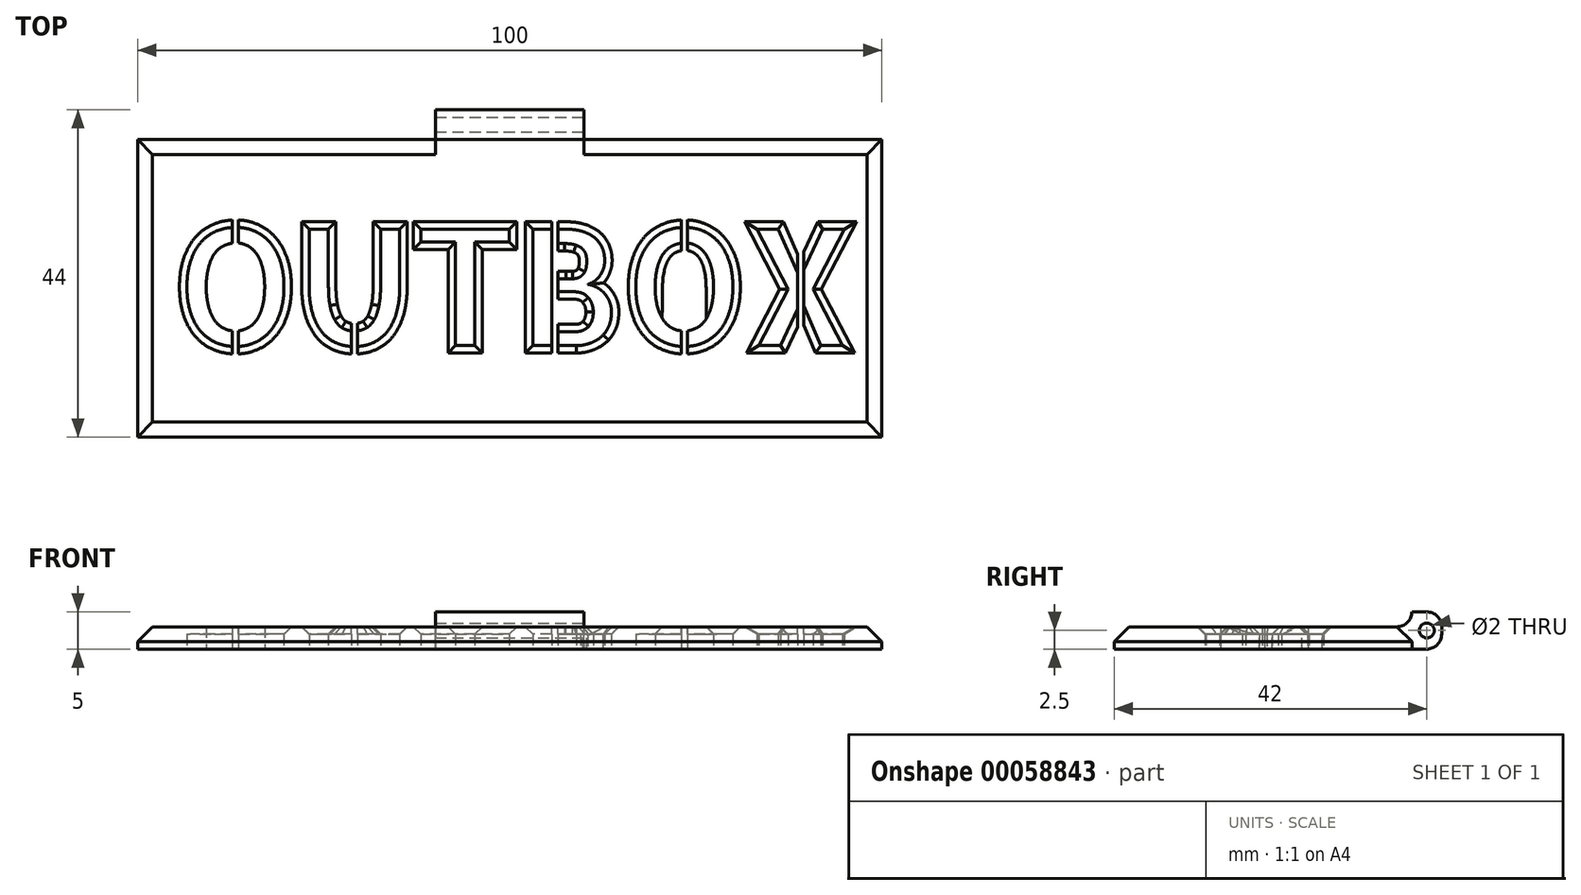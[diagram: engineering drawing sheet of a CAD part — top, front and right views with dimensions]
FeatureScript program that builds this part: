
annotation { "Feature Type Name" : "Feature", "Feature Type Description" : "" }
export const myFeature = defineFeature(function(context is Context, id is Id, definition is map)
    precondition{}
    {
        {
            var Q0;
            Q0=qCreatedBy(makeId("Top.planeOp"),FACE);
            var sketch = newSketch(context, id + "F0", { "sketchPlane" : qUnion([Q0])});
            skLineSegment(sketch, "E0.rect.bottom", {"start": v(-50, 20) * mm, "end": v(-10, 20) * mm});
            skLineSegment(sketch, "E0.rect.top", {"start": v(-50, -20) * mm, "end": v(50, -20) * mm});
            skLineSegment(sketch, "E0.rect.left", {"start": v(-50, 20) * mm, "end": v(-50, -20) * mm});
            skLineSegment(sketch, "E0.rect.right", {"start": v(50, 20) * mm, "end": v(50, -20) * mm});
            skPoint(sketch, "E0.rect.middle", {"position": v(0, 0) * mm});
            skText(sketch, "E1", { "text": "OUTBOX", "fontName": "AllertaStencil-Regular.ttf"});
            skLineSegment(sketch, "E2.rect.bottom", {"start": v(-10, 24) * mm, "end": v(10, 24) * mm});
            skLineSegment(sketch, "E2.rect.left", {"start": v(-10, 24) * mm, "end": v(-10, 20) * mm});
            skLineSegment(sketch, "E2.rect.right", {"start": v(10, 24) * mm, "end": v(10, 20) * mm});
            skPoint(sketch, "E2.rect.middle", {"position": v(0, 20) * mm});
            skPoint(sketch, "E2.rect.top.start.orphan", {"position": v(-10, 16) * mm});
            skPoint(sketch, "E3.orphan", {"position": v(10, 16) * mm});
            skLineSegment(sketch, "E4.trimOffspring", {"start": v(10, 20) * mm, "end": v(50, 20) * mm});
            skLineSegment(sketch, "E5", {"start": v(10, 20) * mm, "end": v(-10, 20) * mm});
            const initialGuessF0  = {"E1": [-0.045, -0.00771, 1, 0, 0.01566]};
            skSetInitialGuess(sketch, initialGuessF0);
            skSolve(sketch);
        }
        {
            var Q0;
            Q0 = qSketchRegion(id + "F0", true);
            extrude(context, id + "F1", {"entities" : qUnion([Q0]), "depth" : 3 * mm});
        }
        {
            var Q0;
            Q0=makeQuery(id+"F0.imprint","IMPRINT",FACE,{"disambiguationData":[TD([[makeQuery(id+"F0.imprint","IMPRINT",EDGE,{"derivedFrom":sQuery(id+"F0.wireOp",EDGE,"E2.rect.bottom")}),-1.0]])]});
            extrude(context, id + "F2", {"entities" : qUnion([Q0]), "operationType" : NewBodyOperationType.ADD, "depth" : 5 * mm});
        }
        {
            var Q0;
            Q0=makeQuery(id+"F2.boolean.opBoolean","INTERSECT",EDGE,{"derivedFrom":[makeQuery(id+"F1.opExtrude","CAP_FACE",FACE,{"disambiguationData":[OSD([sQuery(id+"F0.wireOp",EDGE,"E0.rect.bottom"),sQuery(id+"F0.wireOp",EDGE,"E0.rect.top"),sQuery(id+"F0.wireOp",EDGE,"E0.rect.left"),sQuery(id+"F0.wireOp",EDGE,"E0.rect.right"),sQuery(id+"F0.wireOp",EDGE,"E1.sketch_text.stroke-0"),sQuery(id+"F0.wireOp",EDGE,"E1.sketch_text.stroke-1"),sQuery(id+"F0.wireOp",EDGE,"E1.sketch_text.stroke-2"),sQuery(id+"F0.wireOp",EDGE,"E1.sketch_text.stroke-3"),sQuery(id+"F0.wireOp",EDGE,"E1.sketch_text.stroke-4"),sQuery(id+"F0.wireOp",EDGE,"E1.sketch_text.stroke-5"),sQuery(id+"F0.wireOp",EDGE,"E1.sketch_text.stroke-6"),sQuery(id+"F0.wireOp",EDGE,"E1.sketch_text.stroke-7"),sQuery(id+"F0.wireOp",EDGE,"E1.sketch_text.stroke-8"),sQuery(id+"F0.wireOp",EDGE,"E1.sketch_text.stroke-9"),sQuery(id+"F0.wireOp",EDGE,"E1.sketch_text.stroke-10"),sQuery(id+"F0.wireOp",EDGE,"E1.sketch_text.stroke-11"),sQuery(id+"F0.wireOp",EDGE,"E1.sketch_text.stroke-12"),sQuery(id+"F0.wireOp",EDGE,"E1.sketch_text.stroke-13"),sQuery(id+"F0.wireOp",EDGE,"E1.sketch_text.stroke-14"),sQuery(id+"F0.wireOp",EDGE,"E1.sketch_text.stroke-15"),sQuery(id+"F0.wireOp",EDGE,"E1.sketch_text.stroke-16"),sQuery(id+"F0.wireOp",EDGE,"E1.sketch_text.stroke-17"),sQuery(id+"F0.wireOp",EDGE,"E1.sketch_text.stroke-18"),sQuery(id+"F0.wireOp",EDGE,"E1.sketch_text.stroke-19"),sQuery(id+"F0.wireOp",EDGE,"E1.sketch_text.stroke-20"),sQuery(id+"F0.wireOp",EDGE,"E1.sketch_text.stroke-21"),sQuery(id+"F0.wireOp",EDGE,"E1.sketch_text.stroke-22"),sQuery(id+"F0.wireOp",EDGE,"E1.sketch_text.stroke-23"),sQuery(id+"F0.wireOp",EDGE,"E1.sketch_text.stroke-24"),sQuery(id+"F0.wireOp",EDGE,"E1.sketch_text.stroke-25"),sQuery(id+"F0.wireOp",EDGE,"E1.sketch_text.stroke-26"),sQuery(id+"F0.wireOp",EDGE,"E1.sketch_text.stroke-27"),sQuery(id+"F0.wireOp",EDGE,"E1.sketch_text.stroke-28"),sQuery(id+"F0.wireOp",EDGE,"E1.sketch_text.stroke-29"),sQuery(id+"F0.wireOp",EDGE,"E1.sketch_text.stroke-30"),sQuery(id+"F0.wireOp",EDGE,"E1.sketch_text.stroke-31"),sQuery(id+"F0.wireOp",EDGE,"E1.sketch_text.stroke-32"),sQuery(id+"F0.wireOp",EDGE,"E1.sketch_text.stroke-33"),sQuery(id+"F0.wireOp",EDGE,"E1.sketch_text.stroke-34"),sQuery(id+"F0.wireOp",EDGE,"E1.sketch_text.stroke-35"),sQuery(id+"F0.wireOp",EDGE,"E1.sketch_text.stroke-36"),sQuery(id+"F0.wireOp",EDGE,"E1.sketch_text.stroke-37"),sQuery(id+"F0.wireOp",EDGE,"E1.sketch_text.stroke-38"),sQuery(id+"F0.wireOp",EDGE,"E1.sketch_text.stroke-39"),sQuery(id+"F0.wireOp",EDGE,"E1.sketch_text.stroke-40"),sQuery(id+"F0.wireOp",EDGE,"E1.sketch_text.stroke-41"),sQuery(id+"F0.wireOp",EDGE,"E1.sketch_text.stroke-42"),sQuery(id+"F0.wireOp",EDGE,"E1.sketch_text.stroke-43"),sQuery(id+"F0.wireOp",EDGE,"E1.sketch_text.stroke-44"),sQuery(id+"F0.wireOp",EDGE,"E1.sketch_text.stroke-45"),sQuery(id+"F0.wireOp",EDGE,"E1.sketch_text.stroke-46"),sQuery(id+"F0.wireOp",EDGE,"E1.sketch_text.stroke-47"),sQuery(id+"F0.wireOp",EDGE,"E1.sketch_text.stroke-48"),sQuery(id+"F0.wireOp",EDGE,"E1.sketch_text.stroke-49"),sQuery(id+"F0.wireOp",EDGE,"E1.sketch_text.stroke-50"),sQuery(id+"F0.wireOp",EDGE,"E1.sketch_text.stroke-51"),sQuery(id+"F0.wireOp",EDGE,"E1.sketch_text.stroke-52"),sQuery(id+"F0.wireOp",EDGE,"E1.sketch_text.stroke-53"),sQuery(id+"F0.wireOp",EDGE,"E1.sketch_text.stroke-54"),sQuery(id+"F0.wireOp",EDGE,"E1.sketch_text.stroke-55"),sQuery(id+"F0.wireOp",EDGE,"E1.sketch_text.stroke-56"),sQuery(id+"F0.wireOp",EDGE,"E1.sketch_text.stroke-57"),sQuery(id+"F0.wireOp",EDGE,"E1.sketch_text.stroke-58"),sQuery(id+"F0.wireOp",EDGE,"E1.sketch_text.stroke-59"),sQuery(id+"F0.wireOp",EDGE,"E1.sketch_text.stroke-60"),sQuery(id+"F0.wireOp",EDGE,"E1.sketch_text.stroke-61"),sQuery(id+"F0.wireOp",EDGE,"E1.sketch_text.stroke-62"),sQuery(id+"F0.wireOp",EDGE,"E1.sketch_text.stroke-63"),sQuery(id+"F0.wireOp",EDGE,"E1.sketch_text.stroke-64"),sQuery(id+"F0.wireOp",EDGE,"E1.sketch_text.stroke-65"),sQuery(id+"F0.wireOp",EDGE,"E1.sketch_text.stroke-66"),sQuery(id+"F0.wireOp",EDGE,"E1.sketch_text.stroke-67"),sQuery(id+"F0.wireOp",EDGE,"E1.sketch_text.stroke-68"),sQuery(id+"F0.wireOp",EDGE,"E1.sketch_text.stroke-69"),sQuery(id+"F0.wireOp",EDGE,"E1.sketch_text.stroke-70"),sQuery(id+"F0.wireOp",EDGE,"E1.sketch_text.stroke-71"),sQuery(id+"F0.wireOp",EDGE,"E1.sketch_text.stroke-72"),sQuery(id+"F0.wireOp",EDGE,"E1.sketch_text.stroke-73"),sQuery(id+"F0.wireOp",EDGE,"E1.sketch_text.stroke-74"),sQuery(id+"F0.wireOp",EDGE,"E1.sketch_text.stroke-75"),sQuery(id+"F0.wireOp",EDGE,"E1.sketch_text.stroke-76"),sQuery(id+"F0.wireOp",EDGE,"E1.sketch_text.stroke-77"),sQuery(id+"F0.wireOp",EDGE,"E1.sketch_text.stroke-78"),sQuery(id+"F0.wireOp",EDGE,"E1.sketch_text.stroke-79"),sQuery(id+"F0.wireOp",EDGE,"E1.sketch_text.stroke-80"),sQuery(id+"F0.wireOp",EDGE,"E1.sketch_text.stroke-81"),sQuery(id+"F0.wireOp",EDGE,"E1.sketch_text.stroke-82"),sQuery(id+"F0.wireOp",EDGE,"E1.sketch_text.stroke-83"),sQuery(id+"F0.wireOp",EDGE,"E1.sketch_text.stroke-84"),sQuery(id+"F0.wireOp",EDGE,"E1.sketch_text.stroke-85"),sQuery(id+"F0.wireOp",EDGE,"E1.sketch_text.stroke-86"),sQuery(id+"F0.wireOp",EDGE,"E1.sketch_text.stroke-87"),sQuery(id+"F0.wireOp",EDGE,"E1.sketch_text.stroke-88"),sQuery(id+"F0.wireOp",EDGE,"E1.sketch_text.stroke-89"),sQuery(id+"F0.wireOp",EDGE,"E1.sketch_text.stroke-90"),sQuery(id+"F0.wireOp",EDGE,"E1.sketch_text.stroke-91"),sQuery(id+"F0.wireOp",EDGE,"E1.sketch_text.stroke-92"),sQuery(id+"F0.wireOp",EDGE,"E1.sketch_text.stroke-93"),sQuery(id+"F0.wireOp",EDGE,"E1.sketch_text.stroke-94"),sQuery(id+"F0.wireOp",EDGE,"E1.sketch_text.stroke-95"),sQuery(id+"F0.wireOp",EDGE,"E1.sketch_text.stroke-96"),sQuery(id+"F0.wireOp",EDGE,"E1.sketch_text.stroke-97"),sQuery(id+"F0.wireOp",EDGE,"E1.sketch_text.stroke-98"),sQuery(id+"F0.wireOp",EDGE,"E1.sketch_text.stroke-99"),sQuery(id+"F0.wireOp",EDGE,"E1.sketch_text.stroke-100"),sQuery(id+"F0.wireOp",EDGE,"E1.sketch_text.stroke-101"),sQuery(id+"F0.wireOp",EDGE,"E1.sketch_text.stroke-102"),sQuery(id+"F0.wireOp",EDGE,"E1.sketch_text.stroke-103"),sQuery(id+"F0.wireOp",EDGE,"E1.sketch_text.stroke-104"),sQuery(id+"F0.wireOp",EDGE,"E1.sketch_text.stroke-105"),sQuery(id+"F0.wireOp",EDGE,"E1.sketch_text.stroke-106"),sQuery(id+"F0.wireOp",EDGE,"E1.sketch_text.stroke-107"),sQuery(id+"F0.wireOp",EDGE,"E1.sketch_text.stroke-108"),sQuery(id+"F0.wireOp",EDGE,"E1.sketch_text.stroke-109"),sQuery(id+"F0.wireOp",EDGE,"E1.sketch_text.stroke-110"),sQuery(id+"F0.wireOp",EDGE,"E1.sketch_text.stroke-111"),sQuery(id+"F0.wireOp",EDGE,"E1.sketch_text.stroke-112"),sQuery(id+"F0.wireOp",EDGE,"E1.sketch_text.stroke-113"),sQuery(id+"F0.wireOp",EDGE,"E1.sketch_text.stroke-114"),sQuery(id+"F0.wireOp",EDGE,"E1.sketch_text.stroke-115"),sQuery(id+"F0.wireOp",EDGE,"E1.sketch_text.stroke-116"),sQuery(id+"F0.wireOp",EDGE,"E1.sketch_text.stroke-117"),sQuery(id+"F0.wireOp",EDGE,"E1.sketch_text.stroke-118"),sQuery(id+"F0.wireOp",EDGE,"E1.sketch_text.stroke-119"),sQuery(id+"F0.wireOp",EDGE,"E1.sketch_text.stroke-120"),sQuery(id+"F0.wireOp",EDGE,"E1.sketch_text.stroke-121"),sQuery(id+"F0.wireOp",EDGE,"E1.sketch_text.stroke-122"),sQuery(id+"F0.wireOp",EDGE,"E1.sketch_text.stroke-123"),sQuery(id+"F0.wireOp",EDGE,"E1.sketch_text.stroke-124"),sQuery(id+"F0.wireOp",EDGE,"E1.sketch_text.stroke-125"),sQuery(id+"F0.wireOp",EDGE,"E1.sketch_text.stroke-126"),sQuery(id+"F0.wireOp",EDGE,"E1.sketch_text.stroke-127"),sQuery(id+"F0.wireOp",EDGE,"E1.sketch_text.stroke-128"),sQuery(id+"F0.wireOp",EDGE,"E1.sketch_text.stroke-129"),sQuery(id+"F0.wireOp",EDGE,"E1.sketch_text.stroke-130"),sQuery(id+"F0.wireOp",EDGE,"E1.sketch_text.stroke-131"),sQuery(id+"F0.wireOp",EDGE,"E1.sketch_text.stroke-132"),sQuery(id+"F0.wireOp",EDGE,"E1.sketch_text.stroke-133"),sQuery(id+"F0.wireOp",EDGE,"E1.sketch_text.stroke-134"),sQuery(id+"F0.wireOp",EDGE,"E1.sketch_text.stroke-135"),sQuery(id+"F0.wireOp",EDGE,"E1.sketch_text.stroke-136"),sQuery(id+"F0.wireOp",EDGE,"E1.sketch_text.stroke-137"),sQuery(id+"F0.wireOp",EDGE,"E1.sketch_text.stroke-138"),sQuery(id+"F0.wireOp",EDGE,"E1.sketch_text.stroke-139"),sQuery(id+"F0.wireOp",EDGE,"E1.sketch_text.stroke-140"),sQuery(id+"F0.wireOp",EDGE,"E1.sketch_text.stroke-141"),sQuery(id+"F0.wireOp",EDGE,"E1.sketch_text.stroke-142"),sQuery(id+"F0.wireOp",EDGE,"E1.sketch_text.stroke-143"),sQuery(id+"F0.wireOp",EDGE,"E1.sketch_text.stroke-144"),sQuery(id+"F0.wireOp",EDGE,"E1.sketch_text.stroke-145"),sQuery(id+"F0.wireOp",EDGE,"E1.sketch_text.stroke-146"),sQuery(id+"F0.wireOp",EDGE,"E1.sketch_text.stroke-147"),sQuery(id+"F0.wireOp",EDGE,"E1.sketch_text.stroke-148"),sQuery(id+"F0.wireOp",EDGE,"E1.sketch_text.stroke-149"),sQuery(id+"F0.wireOp",EDGE,"E1.sketch_text.stroke-150"),sQuery(id+"F0.wireOp",EDGE,"E1.sketch_text.stroke-151"),sQuery(id+"F0.wireOp",EDGE,"E1.sketch_text.stroke-152"),sQuery(id+"F0.wireOp",EDGE,"E1.sketch_text.stroke-153"),sQuery(id+"F0.wireOp",EDGE,"E1.sketch_text.stroke-154"),sQuery(id+"F0.wireOp",EDGE,"E1.sketch_text.stroke-155"),sQuery(id+"F0.wireOp",EDGE,"E1.sketch_text.stroke-156"),sQuery(id+"F0.wireOp",EDGE,"E1.sketch_text.stroke-157"),sQuery(id+"F0.wireOp",EDGE,"E1.sketch_text.stroke-158"),sQuery(id+"F0.wireOp",EDGE,"E1.sketch_text.stroke-159"),sQuery(id+"F0.wireOp",EDGE,"E1.sketch_text.stroke-160"),sQuery(id+"F0.wireOp",EDGE,"E2.rect.bottom"),sQuery(id+"F0.wireOp",EDGE,"E2.rect.left"),sQuery(id+"F0.wireOp",EDGE,"E2.rect.right"),sQuery(id+"F0.wireOp",EDGE,"E4.trimOffspring")])],"isStart":false}),makeQuery(id+"F2.opExtrude","SWEPT_FACE",FACE,{"disambiguationData":[OSD([sQuery(id+"F0.wireOp",EDGE,"E5")])]})]});
            fillet(context, id + "F3", {"entities" : qUnion([Q0]), "radius" : 2 * mm, "tangentPropagation" : true, "allowEdgeOverflow" : false});
        }
        {
            var Q0;
            {var subQ0=sQuery(id+"F0.wireOp",EDGE,"E2.rect.right");Q0=makeQuery(id+"F2.boolean.opBoolean","MERGE",FACE,{"derivedFrom":[makeQuery(id+"F1.opExtrude","SWEPT_FACE",FACE,{"disambiguationData":[OSD([subQ0])]}),makeQuery(id+"F2.opExtrude","SWEPT_FACE",FACE,{"disambiguationData":[OSD([subQ0])]})]});}
            var sketch = newSketch(context, id + "F4", { "sketchPlane" : qUnion([Q0])});
            skCircle(sketch, "E6", {"center": v(22, 2.5) * mm, "radius": 1 * mm});
            skLineSegment(sketch, "E7", {"start": v(24, 2.5) * mm, "end": v(22, 2.5) * mm, "construction": true});
            skLineSegment(sketch, "E8", {"start": v(22, 5) * mm, "end": v(22, 2.5) * mm, "construction": true});
            skPoint(sketch, "E9.trimOffspring.end.orphan", {"position": v(22, 0) * mm});
            skSolve(sketch);
        }
        {
            var Q0;
            Q0=makeQuery(id+"F1.opExtrude","CAP_EDGE",EDGE,{"disambiguationData":[OSD([sQuery(id+"F0.wireOp",EDGE,"E1.sketch_text.stroke-3")])],"isStart":false});
            var Q1;
            Q1=makeQuery(id+"F1.opExtrude","CAP_EDGE",EDGE,{"disambiguationData":[OSD([sQuery(id+"F0.wireOp",EDGE,"E1.sketch_text.stroke-18")])],"isStart":false});
            var Q2;
            Q2=makeQuery(id+"F1.opExtrude","CAP_EDGE",EDGE,{"disambiguationData":[OSD([sQuery(id+"F0.wireOp",EDGE,"E1.sketch_text.stroke-45")])],"isStart":false});
            var Q3;
            Q3=makeQuery(id+"F1.opExtrude","CAP_EDGE",EDGE,{"disambiguationData":[OSD([sQuery(id+"F0.wireOp",EDGE,"E1.sketch_text.stroke-47")])],"isStart":false});
            var Q4;
            Q4=makeQuery(id+"F1.opExtrude","CAP_EDGE",EDGE,{"disambiguationData":[OSD([sQuery(id+"F0.wireOp",EDGE,"E1.sketch_text.stroke-58")])],"isStart":false});
            var Q5;
            Q5=makeQuery(id+"F1.opExtrude","CAP_EDGE",EDGE,{"disambiguationData":[OSD([sQuery(id+"F0.wireOp",EDGE,"E1.sketch_text.stroke-48")])],"isStart":false});
            var Q6;
            Q6=makeQuery(id+"F1.opExtrude","CAP_EDGE",EDGE,{"disambiguationData":[OSD([sQuery(id+"F0.wireOp",EDGE,"E1.sketch_text.stroke-66")])],"isStart":false});
            var Q7;
            Q7=makeQuery(id+"F1.opExtrude","CAP_EDGE",EDGE,{"disambiguationData":[OSD([sQuery(id+"F0.wireOp",EDGE,"E1.sketch_text.stroke-65")])],"isStart":false});
            var Q8;
            Q8=makeQuery(id+"F1.opExtrude","CAP_EDGE",EDGE,{"disambiguationData":[OSD([sQuery(id+"F0.wireOp",EDGE,"E1.sketch_text.stroke-64")])],"isStart":false});
            var Q9;
            Q9=makeQuery(id+"F1.opExtrude","CAP_EDGE",EDGE,{"disambiguationData":[OSD([sQuery(id+"F0.wireOp",EDGE,"E1.sketch_text.stroke-62")])],"isStart":false});
            var Q10;
            Q10=makeQuery(id+"F1.opExtrude","CAP_EDGE",EDGE,{"disambiguationData":[OSD([sQuery(id+"F0.wireOp",EDGE,"E1.sketch_text.stroke-59")])],"isStart":false});
            var Q11;
            Q11=makeQuery(id+"F1.opExtrude","CAP_EDGE",EDGE,{"disambiguationData":[OSD([sQuery(id+"F0.wireOp",EDGE,"E1.sketch_text.stroke-46")])],"isStart":false});
            var Q12;
            Q12=makeQuery(id+"F1.opExtrude","CAP_EDGE",EDGE,{"disambiguationData":[OSD([sQuery(id+"F0.wireOp",EDGE,"E1.sketch_text.stroke-67")])],"isStart":false});
            var Q13;
            Q13=makeQuery(id+"F1.opExtrude","CAP_EDGE",EDGE,{"disambiguationData":[OSD([sQuery(id+"F0.wireOp",EDGE,"E1.sketch_text.stroke-60")])],"isStart":false});
            var Q14;
            Q14=makeQuery(id+"F1.opExtrude","CAP_EDGE",EDGE,{"disambiguationData":[OSD([sQuery(id+"F0.wireOp",EDGE,"E1.sketch_text.stroke-61")])],"isStart":false});
            var Q15;
            Q15=makeQuery(id+"F1.opExtrude","CAP_EDGE",EDGE,{"disambiguationData":[OSD([sQuery(id+"F0.wireOp",EDGE,"E1.sketch_text.stroke-110")])],"isStart":false});
            var Q16;
            Q16=makeQuery(id+"F1.opExtrude","CAP_EDGE",EDGE,{"disambiguationData":[OSD([sQuery(id+"F0.wireOp",EDGE,"E1.sketch_text.stroke-107")])],"isStart":false});
            var Q17;
            Q17=makeQuery(id+"F1.opExtrude","CAP_EDGE",EDGE,{"disambiguationData":[OSD([sQuery(id+"F0.wireOp",EDGE,"E1.sketch_text.stroke-98")])],"isStart":false});
            var Q18;
            Q18=makeQuery(id+"F1.opExtrude","CAP_EDGE",EDGE,{"disambiguationData":[OSD([sQuery(id+"F0.wireOp",EDGE,"E1.sketch_text.stroke-95")])],"isStart":false});
            var Q19;
            Q19=makeQuery(id+"F1.opExtrude","CAP_EDGE",EDGE,{"disambiguationData":[OSD([sQuery(id+"F0.wireOp",EDGE,"E1.sketch_text.stroke-85")])],"isStart":false});
            var Q20;
            Q20=makeQuery(id+"F1.opExtrude","CAP_EDGE",EDGE,{"disambiguationData":[OSD([sQuery(id+"F0.wireOp",EDGE,"E1.sketch_text.stroke-78")])],"isStart":false});
            var Q21;
            Q21=makeQuery(id+"F1.opExtrude","CAP_EDGE",EDGE,{"disambiguationData":[OSD([sQuery(id+"F0.wireOp",EDGE,"E1.sketch_text.stroke-109")])],"isStart":false});
            var Q22;
            Q22=makeQuery(id+"F1.opExtrude","CAP_EDGE",EDGE,{"disambiguationData":[OSD([sQuery(id+"F0.wireOp",EDGE,"E1.sketch_text.stroke-114")])],"isStart":false});
            var Q23;
            Q23=makeQuery(id+"F1.opExtrude","CAP_EDGE",EDGE,{"disambiguationData":[OSD([sQuery(id+"F0.wireOp",EDGE,"E1.sketch_text.stroke-116")])],"isStart":false});
            var Q24;
            Q24=makeQuery(id+"F1.opExtrude","CAP_EDGE",EDGE,{"disambiguationData":[OSD([sQuery(id+"F0.wireOp",EDGE,"E1.sketch_text.stroke-129")])],"isStart":false});
            var Q25;
            Q25=makeQuery(id+"F1.opExtrude","CAP_EDGE",EDGE,{"disambiguationData":[OSD([sQuery(id+"F0.wireOp",EDGE,"E1.sketch_text.stroke-144")])],"isStart":false});
            var Q26;
            Q26=makeQuery(id+"F1.opExtrude","CAP_EDGE",EDGE,{"disambiguationData":[OSD([sQuery(id+"F0.wireOp",EDGE,"E1.sketch_text.stroke-153")])],"isStart":false});
            var Q27;
            Q27=makeQuery(id+"F1.opExtrude","CAP_EDGE",EDGE,{"disambiguationData":[OSD([sQuery(id+"F0.wireOp",EDGE,"E1.sketch_text.stroke-152")])],"isStart":false});
            var Q28;
            Q28=makeQuery(id+"F1.opExtrude","CAP_EDGE",EDGE,{"disambiguationData":[OSD([sQuery(id+"F0.wireOp",EDGE,"E1.sketch_text.stroke-156")])],"isStart":false});
            var Q29;
            Q29=makeQuery(id+"F1.opExtrude","CAP_EDGE",EDGE,{"disambiguationData":[OSD([sQuery(id+"F0.wireOp",EDGE,"E1.sketch_text.stroke-155")])],"isStart":false});
            var Q30;
            Q30=makeQuery(id+"F1.opExtrude","CAP_EDGE",EDGE,{"disambiguationData":[OSD([sQuery(id+"F0.wireOp",EDGE,"E1.sketch_text.stroke-154")])],"isStart":false});
            var Q31;
            Q31=makeQuery(id+"F1.opExtrude","CAP_EDGE",EDGE,{"disambiguationData":[OSD([sQuery(id+"F0.wireOp",EDGE,"E1.sketch_text.stroke-160")])],"isStart":false});
            var Q32;
            Q32=makeQuery(id+"F1.opExtrude","CAP_EDGE",EDGE,{"disambiguationData":[OSD([sQuery(id+"F0.wireOp",EDGE,"E1.sketch_text.stroke-147")])],"isStart":false});
            var Q33;
            Q33=makeQuery(id+"F1.opExtrude","CAP_EDGE",EDGE,{"disambiguationData":[OSD([sQuery(id+"F0.wireOp",EDGE,"E1.sketch_text.stroke-151")])],"isStart":false});
            var Q34;
            Q34=makeQuery(id+"F1.opExtrude","CAP_EDGE",EDGE,{"disambiguationData":[OSD([sQuery(id+"F0.wireOp",EDGE,"E1.sketch_text.stroke-148")])],"isStart":false});
            var Q35;
            Q35=makeQuery(id+"F1.opExtrude","CAP_EDGE",EDGE,{"disambiguationData":[OSD([sQuery(id+"F0.wireOp",EDGE,"E1.sketch_text.stroke-159")])],"isStart":false});
            var Q36;
            Q36=makeQuery(id+"F1.opExtrude","CAP_EDGE",EDGE,{"disambiguationData":[OSD([sQuery(id+"F0.wireOp",EDGE,"E1.sketch_text.stroke-150")])],"isStart":false});
            var Q37;
            Q37=makeQuery(id+"F1.opExtrude","CAP_EDGE",EDGE,{"disambiguationData":[OSD([sQuery(id+"F0.wireOp",EDGE,"E1.sketch_text.stroke-157")])],"isStart":false});
            var Q38;
            Q38=makeQuery(id+"F1.opExtrude","CAP_EDGE",EDGE,{"disambiguationData":[OSD([sQuery(id+"F0.wireOp",EDGE,"E1.sketch_text.stroke-63")])],"isStart":false});
            chamfer(context, id + "F5", {"entities" : qUnion([Q0, Q1, Q2, Q3, Q4, Q5, Q6, Q7, Q8, Q9, Q10, Q11, Q12, Q13, Q14, Q15, Q16, Q17, Q18, Q19, Q20, Q21, Q22, Q23, Q24, Q25, Q26, Q27, Q28, Q29, Q30, Q31, Q32, Q33, Q34, Q35, Q36, Q37, Q38]), "width" : 1 * mm, "tangentPropagation" : true});
        }
        {
            var Q0;
            Q0=makeQuery(id+"F1.opExtrude","CAP_EDGE",EDGE,{"disambiguationData":[OSD([sQuery(id+"F0.wireOp",EDGE,"E0.rect.bottom")])],"isStart":false});
            var Q1;
            Q1=makeQuery(id+"F1.opExtrude","CAP_EDGE",EDGE,{"disambiguationData":[OSD([sQuery(id+"F0.wireOp",EDGE,"E4.trimOffspring")])],"isStart":false});
            var Q2;
            Q2=makeQuery(id+"F1.opExtrude","CAP_EDGE",EDGE,{"disambiguationData":[OSD([sQuery(id+"F0.wireOp",EDGE,"E0.rect.right")])],"isStart":false});
            var Q3;
            Q3=makeQuery(id+"F1.opExtrude","CAP_EDGE",EDGE,{"disambiguationData":[OSD([sQuery(id+"F0.wireOp",EDGE,"E0.rect.top")])],"isStart":false});
            var Q4;
            Q4=makeQuery(id+"F1.opExtrude","CAP_EDGE",EDGE,{"disambiguationData":[OSD([sQuery(id+"F0.wireOp",EDGE,"E0.rect.left")])],"isStart":false});
            chamfer(context, id + "F6", {"entities" : qUnion([Q0, Q1, Q2, Q3, Q4]), "width" : 2 * mm, "tangentPropagation" : true});
        }
        {
            var Q0;
            Q0=makeQuery(id+"F2.opExtrude","CAP_EDGE",EDGE,{"disambiguationData":[OSD([sQuery(id+"F0.wireOp",EDGE,"E2.rect.bottom")])],"isStart":false});
            var Q1;
            Q1=makeQuery(id+"F1.opExtrude","CAP_EDGE",EDGE,{"disambiguationData":[OSD([sQuery(id+"F0.wireOp",EDGE,"E2.rect.bottom")])],"isStart":true});
            fillet(context, id + "F7", {"entities" : qUnion([Q0, Q1]), "radius" : 2 * mm, "tangentPropagation" : true, "allowEdgeOverflow" : false});
        }
        {
            var Q0;
            Q0 = qSketchRegion(id + "F4", true);
            extrude(context, id + "F8", {"entities" : qUnion([Q0]), "operationType" : NewBodyOperationType.REMOVE, "endBound" : BoundingType.THROUGH_ALL, "oppositeDirection" : true, "depth" : 25 * mm});
        }
    });
